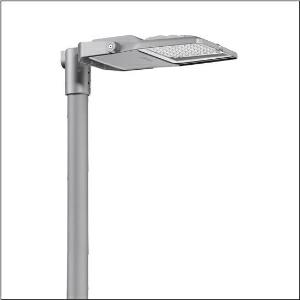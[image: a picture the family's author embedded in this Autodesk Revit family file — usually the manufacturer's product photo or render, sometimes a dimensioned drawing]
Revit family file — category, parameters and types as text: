
# Revit family: floodlight_fl_21_iq_mini___pl33t_5xa7772d4f3a_7ca2
name_source: partatom
category: Lighting Fixtures
units: mm (PartAtom-declared; Revit-internal decimal feet)

## family parameters
Cut with Voids When Loaded = No
Host = Face
Light Source = No
Part Type = Normal
Room Calculation Point = No
Round Connector Dimension = Use Diameter
Shared = No

## types (1)
- --- (1 x LED, 18390 lm, 143 W, 4000K)
    Apparent Load = 143 VA
    CIE Flux Codes = 26 75 99 100 100
    Color Rendering = 70
    Color Temperature = 4000K
    Default Elevation = 1800 mm
    Description = Floodlight FL 21 iQ mini, floodlight, primary light control with lens, of PMMA, primary optical cover: protective disc, of toughened safety glass, transparent, light distribution: PL33T, light emission: direct distribution, installation type: surface-mounted, lamps: LED, High Power LED, rated values: 18.390lm | 143W | 128,6lm/W (begin service life); end service life: 18.390lm | 151,6W; at 50% lumin. flux: 9.195lm | 60,8W | 151,2lm/W, colour temperature: 4000K, colour rendering: CRI > 70, light colour: 740, light setting 1 begin service life: 100% | 18.390lm | 143W | 128,6lm/W | 4.000K, light setting 1 end service life: 151,6W, further light settings possible, control: pre-setting: linear dimming characteristic, Auto-Match, Temp-Guard, Night-Set, Smart-Wire, Desk-Remote (wireless, voltage-free reading and setting of iQ features in the workshop via application-optimized NFC function/RFID function), optimised constant luminous flux control (CLO 2.0), Light-Fading, Lumen-Switch, with terminal, 6-pole, mains connection: 220..240V, AC, 50/60Hz, luminaire housing, of diecast aluminium, powder-coated, SITECO metallic grey (DB 702S), corrosivity category C5 mid according to DIN EN ISO 12944suitable for swimming poolschlorine-resistant, sealing non-destructively replaceable, please order mast flange separately, mast bracket, of steel, galvanised, powder-coated, protection rating (complete): IP66, insulation class (complete): insulation class II (safety insulation), certification: CE, ENEC, VDE, protection symbol: D, impact resistance: IK08, permissible operating ambient temperature: -40..+40°C, permissible operating ambient temperature for outdoor applications: -40..+50°C, standard: DIN EN 12944, LABS conformity tested according to VDMA 24364:2018-05, packaging unit: 1 piece

Light Distribution: PL33T
    Height = 70 mm
    Lamp = 1 x LED
    Lamp Light Flux = 18390 lm
    Lamp Power = 143 W
    Lamp count = 1
    Length = 485 mm
    Luminous efficacy = 129 lm/W
    Manufacturer = Siteco
    ModVariant = No
    Model = 5XA7772D4F3A
    Mounting Place = Pole
    Mounting Type = Pole annexe
    Number of Poles = 1
    OnlyDefault = Yes
    Power Factor = 1
    Product Name = Floodlight FL 21 iQ mini | PL33T
    Product group = floodlight | pylon annexe
    ProductGroupID = 6201
    Protection Class = Protection class II
    Protection Degree = IP 66
    RLX_Detail_Level = 1
    RLX_Emergency_Light_Flux = 0 lm
    RLX_Emergency_Type = 0
    RLX_Emergency_Type_DB = No
    RlxData = <blob elided: 101717 chars, md5=108e9fb3>
    Socket = socket
    Standby Power = 0 W
    System Light Flux = 18390 lm
    System Power = 143 W
    Type Comments = factory setting: luminous flux: 100 % | dim-lin: 254 | 730 mA
    Type Image = l_1007125.jpg
    URL = http://relux.com
    VarID = @adj_149831
    Voltage = 0 V
    Weight = 0.00 kg
    Width = 337 mm

## geometry (parser evidence)
native form markers: Blend x4, Sweep x13
no freeform markers — native parametric forms only
